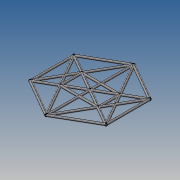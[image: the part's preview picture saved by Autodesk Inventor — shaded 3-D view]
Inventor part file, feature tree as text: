
AUTODESK INVENTOR PART (.ipt)
format: ipt  version: 2015 SP1 (Build 190203100, 203)  size: 1,064,960 bytes
history: native  units: mm
features: extrude x22, other x5, sketch x1, fillet x1, pattern_circular x1
ambient origin geometry x8: Origin, YZ Plane, XZ Plane, XY Plane, X Axis, Y Axis, Z Axis, Center Point
bodies: Solid1 (feature_tree), Solid3 (feature_tree), Solid4 (feature_tree), Solid5 (feature_tree), Solid6 (feature_tree), Solid7 (feature_tree), Solid8 (feature_tree), Solid9 (feature_tree), Solid11 (feature_tree), Solid12 (feature_tree), Solid13 (feature_tree), Solid14 (feature_tree), Solid16 (feature_tree), Solid17 (feature_tree), Solid18 (feature_tree), Solid19 (feature_tree), Solid20 (feature_tree), Solid21 (feature_tree), Solid22 (feature_tree), Solid23 (feature_tree), Solid24 (feature_tree), Solid25 (feature_tree), Solid26 (feature_tree), Solid27 (feature_tree), Solid28 (feature_tree), Solid29 (feature_tree), Solid30 (feature_tree)
feature tree (30):
  sketch  "Sketch1"  dims[d5=30.0mm d8=1.0mm d9=0.5mm d10=0.5mm d11=0.5mm d16=1.0mm d17=0.0mm d20=0.49mm d21=60.0mm d22=360.0deg d25=0.5mm d26=0.5mm d27=1.0mm d28=0.5mm d29=0.5mm d30=0.5mm d31=1.0mm d32=0.5mm d33=1.0mm d34=0.0mm d35=1.0mm d36=0.0mm d38=0.5mm d39=1.0mm d40=0.5mm d41=0.5mm d42=1.0mm d44=0.5mm d45=0.5mm d46=0.5mm d47=0.5mm d48=0.5mm d49=0.5mm d50=0.5mm d51=0.5mm d52=0.5mm d53=0.5mm d54=1.0mm d55=0.0mm d56=1.0mm d57=0.0mm d58=1.0mm d59=0.0mm d60=1.0mm d61=0.0mm d62=0.5mm d63=1.0mm d64=0.5mm d65=0.5mm d66=1.0mm d67=0.0mm d68=0.5mm d69=1.0mm d70=0.5mm d71=0.5mm d72=0.5mm d73=1.0mm d74=0.5mm d75=0.5mm d76=0.5mm d79=0.5mm d81=0.5mm d82=1.0mm d83=0.5mm d84=1.0mm d85=0.0mm d86=1.0mm d87=0.0mm d88=1.0mm d89=0.0mm d90=1.0mm d91=0.0mm d92=0.5mm d93=0.5mm d94=0.5mm d95=1.0mm d96=1.0mm d97=0.0mm d98=0.5mm d99=0.5mm d100=1.0mm d101=0.5mm d102=0.5mm d103=1.0mm d104=0.5mm d105=0.5mm d106=0.5mm d107=1.0mm d108=0.5mm d109=0.5mm d110=0.5mm d111=0.5mm d112=0.5mm d113=1.0mm d114=0.5mm d115=0.5mm d116=1.0mm d117=0.5mm d118=0.5mm d119=0.5mm d120=0.5mm d121=1.0mm d122=0.5mm d123=0.5mm d124=0.5mm d125=1.0mm d126=0.5mm d127=0.5mm d128=0.5mm d129=1.0mm d130=0.5mm d131=1.0mm d132=0.0mm d133=1.0mm d134=0.0mm d135=1.0mm d136=0.0mm d137=1.0mm d138=0.0mm d139=1.0mm d140=0.0mm d141=1.0mm d142=0.0mm d143=1.0mm d144=0.0mm d145=0.5mm d146=0.5mm d147=1.0mm d148=0.5mm d149=0.5mm d150=0.5mm d151=1.0mm d152=0.5mm d153=0.5mm d154=1.0mm d155=0.0mm d156=1.0mm d157=0.0mm]
  extrude  "Extrusion1"  Depth=1.0mm
  extrude  "Extrusion3"  Depth=1.0mm
  extrude  "Extrusion4"  Depth=1.0mm
  extrude  "Extrusion5"  Depth=1.0mm
  extrude  "Extrusion6"  Depth=1.0mm
  extrude  "Extrusion7"  TaperAngle=0.0deg  [1 undecoded]
  extrude  "Extrusion8"  Depth=0.49mm
  extrude  "Extrusion9"  Depth=1.0mm TaperAngle=360.0deg
  extrude  "Extrusion10"  Depth=1.0mm
  extrude  "Extrusion11"  Depth=1.0mm
  extrude  "Extrusion12"  Depth=1.0mm
  extrude  "Extrusion13"  Depth=1.0mm
  extrude  "Extrusion14"  Depth=1.0mm
  extrude  "Extrusion15"  Depth=1.0mm
  extrude  "Extrusion16"  Depth=1.0mm
  extrude  "Extrusion17"  Depth=1.0mm
  extrude  "Extrusion18"  Depth=1.0mm
  extrude  "Extrusion19"  TaperAngle=0.0deg  [1 undecoded]
  extrude  "Extrusion20"  Depth=1.0mm
  extrude  "Extrusion21"  TaperAngle=0.0deg  [1 undecoded]
  extrude  "Extrusion22"  Depth=1.0mm
  extrude  "Extrusion23"  Depth=1.0mm
  fillet  "Fillet1"  Radius=0.5mm
  pattern_circular  "Circular Pattern1"  [2 undecoded]
  other  "Pattern of Solid1:1"
  other  "Pattern of Solid1:2"
  other  "Pattern of Solid1:3"
  other  "Pattern of Solid1:4"
  other  "Pattern of Solid1:5"
note: 5 required parameter values undecoded (feature->parameter linkage not recoverable at this tier; creation-order binding heuristic only, values carry confidence <= 0.55)
